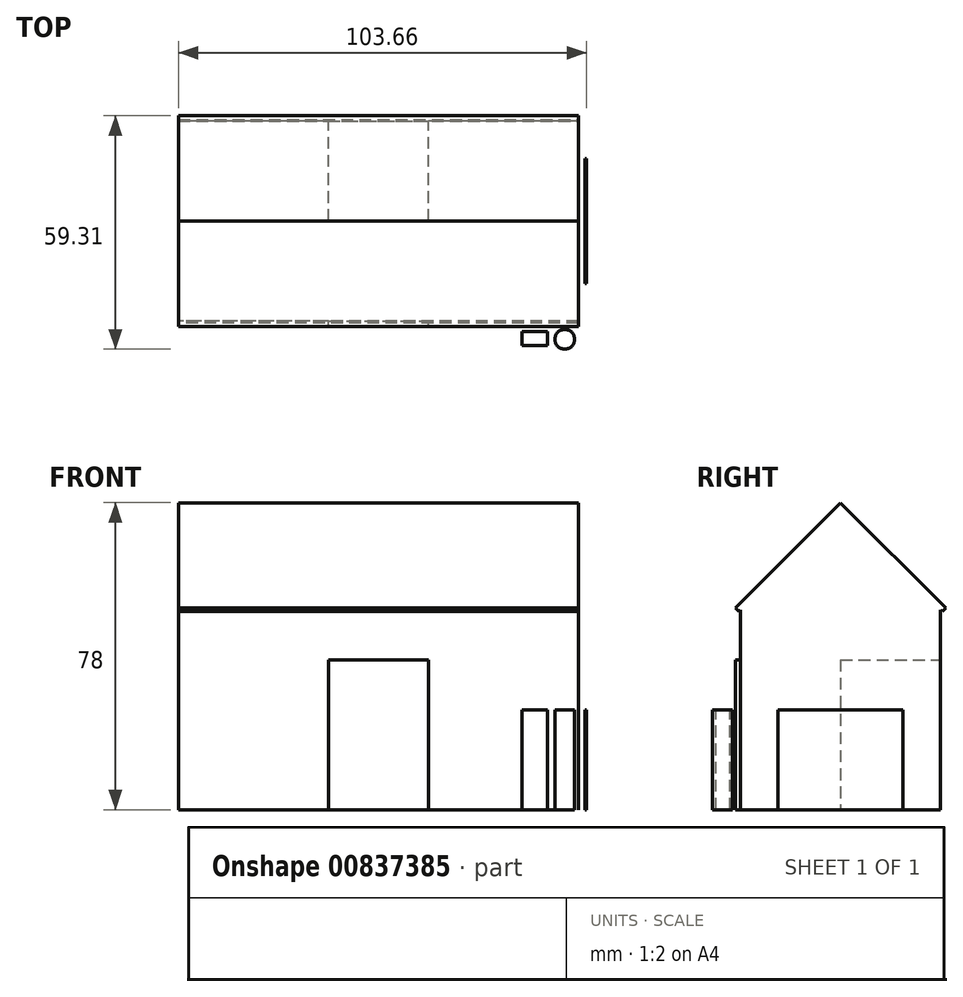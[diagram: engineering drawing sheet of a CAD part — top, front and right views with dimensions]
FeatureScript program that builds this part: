
annotation { "Feature Type Name" : "Feature", "Feature Type Description" : "" }
export const myFeature = defineFeature(function(context is Context, id is Id, definition is map)
    precondition{}
    {
        {
            var Q0;
            Q0=qCreatedBy(makeId("Front.planeOp"),FACE);
            var sketch = newSketch(context, id + "F0", { "sketchPlane" : qUnion([Q0])});
            skLineSegment(sketch, "E0.bottom", {"start": v(50.8, 25.4) * mm, "end": v(-50.8, 25.4) * mm});
            skLineSegment(sketch, "E0.top", {"start": v(50.8, -25.4) * mm, "end": v(-50.8, -25.4) * mm});
            skLineSegment(sketch, "E0.left", {"start": v(50.8, 25.4) * mm, "end": v(50.8, -25.4) * mm});
            skLineSegment(sketch, "E0.right", {"start": v(-50.8, 25.4) * mm, "end": v(-50.8, -25.4) * mm});
            skPoint(sketch, "E0.middle", {"position": v(0, 0) * mm});
            skLineSegment(sketch, "E1.bottom", {"start": v(-50.8, 25.4) * mm, "end": v(50.8, 25.4) * mm});
            skLineSegment(sketch, "E1.top", {"start": v(-50.8, 50.8) * mm, "end": v(50.8, 50.8) * mm});
            skLineSegment(sketch, "E1.left", {"start": v(-50.8, 25.4) * mm, "end": v(-50.8, 50.8) * mm});
            skLineSegment(sketch, "E1.right", {"start": v(50.8, 25.4) * mm, "end": v(50.8, 50.8) * mm});
            skLineSegment(sketch, "E2.bottom", {"start": v(-12.7, 12.7) * mm, "end": v(12.7, 12.7) * mm});
            skLineSegment(sketch, "E3", {"start": v(-12.7, -12.7) * mm, "end": v(-12.7, -25.4) * mm});
            skLineSegment(sketch, "E4", {"start": v(12.7, -12.7) * mm, "end": v(12.7, -25.4) * mm});
            skLineSegment(sketch, "E5", {"start": v(-12.7, 12.7) * mm, "end": v(-12.7, -25.4) * mm});
            skLineSegment(sketch, "E6", {"start": v(12.7, 12.7) * mm, "end": v(12.7, -25.4) * mm});
            skSolve(sketch);
        }
        {
            var Q0;
            Q0=makeQuery(id+"F0.imprint","IMPRINT",FACE,{"disambiguationData":[TD([[makeQuery(id+"F0.imprint","IMPRINT",EDGE,{"derivedFrom":sQuery(id+"F0.wireOp",EDGE,"E0.bottom")}),1.0]])]});
            var Q1;
            Q1=makeQuery(id+"F0.imprint","IMPRINT",FACE,{"disambiguationData":[TD([[makeQuery(id+"F0.imprint","IMPRINT",EDGE,{"derivedFrom":sQuery(id+"F0.wireOp",EDGE,"E0.bottom")}),-1.0]])]});
            extrude(context, id + "F1", {"entities" : qUnion([Q0, Q1]), "endBound" : BoundingType.SYMMETRIC, "depth" : 50.8 * mm, "offsetDistance" : 25.4 * mm});
        }
        {
            var Q0;
            Q0=makeQuery(id+"F1.opExtrude","CAP_EDGE",EDGE,{"disambiguationData":[OSD([sQuery(id+"F0.wireOp",EDGE,"E1.top")])],"isStart":false});
            var Q1;
            Q1=makeQuery(id+"F1.opExtrude","CAP_EDGE",EDGE,{"disambiguationData":[OSD([sQuery(id+"F0.wireOp",EDGE,"E1.top")])],"isStart":true});
            chamfer(context, id + "F2", {"entities" : qUnion([Q0, Q1]), "width" : 25.4 * mm, "tangentPropagation" : true});
        }
        {
            var Q0;
            {var subQ0=sQuery(id+"F0.wireOp",EDGE,"E1.top");Q0=makeQuery(id+"F2.opChamfer","BLEND_FACE",FACE,{"disambiguationData":[OSD([subQ0]),TDD([makeQuery(id+"F1.opExtrude","CAP_EDGE",EDGE,{"disambiguationData":[OSD([subQ0])],"isStart":false})])]});}
            extrude(context, id + "F3", {"entities" : qUnion([Q0]), "operationType" : NewBodyOperationType.ADD, "depth" : 1.27 * mm, "offsetDistance" : 25.4 * mm});
        }
        {
            var Q0;
            {var subQ0=sQuery(id+"F0.wireOp",EDGE,"E1.top");Q0=makeQuery(id+"F3.boolean.opBoolean","MERGE",FACE,{"derivedFrom":[makeQuery(id+"F2.opChamfer","BLEND_FACE",FACE,{"disambiguationData":[OSD([subQ0]),TDD([makeQuery(id+"F1.opExtrude","CAP_EDGE",EDGE,{"disambiguationData":[OSD([subQ0])],"isStart":true})])]}),makeQuery(id+"F3.opExtrude","SWEPT_FACE",FACE,{"disambiguationData":[OSD([subQ0])]})]});}
            extrude(context, id + "F4", {"entities" : qUnion([Q0]), "operationType" : NewBodyOperationType.ADD, "depth" : 1.27 * mm, "offsetDistance" : 25.4 * mm});
        }
        {
            var Q0;
            Q0=makeQuery(id+"F3.opExtrude","SWEPT_FACE",FACE,{"disambiguationData":[OSD([sQuery(id+"F0.wireOp",EDGE,"E0.top"),sQuery(id+"F0.wireOp",EDGE,"E0.left"),sQuery(id+"F0.wireOp",EDGE,"E0.right"),sQuery(id+"F0.wireOp",EDGE,"E1.top"),sQuery(id+"F0.wireOp",EDGE,"E1.left"),sQuery(id+"F0.wireOp",EDGE,"E1.right"),sQuery(id+"F0.wireOp",EDGE,"E2.bottom"),sQuery(id+"F0.wireOp",EDGE,"E3"),sQuery(id+"F0.wireOp",EDGE,"E4"),sQuery(id+"F0.wireOp",EDGE,"E5"),sQuery(id+"F0.wireOp",EDGE,"E6")])]});
            extrude(context, id + "F5", {"entities" : qUnion([Q0]), "operationType" : NewBodyOperationType.ADD, "depth" : 0.64 * mm, "offsetDistance" : 25.4 * mm});
        }
        {
            var Q0;
            Q0=makeQuery(id+"F4.opExtrude","SWEPT_FACE",FACE,{"disambiguationData":[OSD([sQuery(id+"F0.wireOp",EDGE,"E0.top"),sQuery(id+"F0.wireOp",EDGE,"E0.left"),sQuery(id+"F0.wireOp",EDGE,"E0.right"),sQuery(id+"F0.wireOp",EDGE,"E1.top"),sQuery(id+"F0.wireOp",EDGE,"E1.left"),sQuery(id+"F0.wireOp",EDGE,"E1.right"),sQuery(id+"F0.wireOp",EDGE,"E2.bottom"),sQuery(id+"F0.wireOp",EDGE,"E3"),sQuery(id+"F0.wireOp",EDGE,"E4"),sQuery(id+"F0.wireOp",EDGE,"E5"),sQuery(id+"F0.wireOp",EDGE,"E6")])]});
            extrude(context, id + "F6", {"entities" : qUnion([Q0]), "operationType" : NewBodyOperationType.ADD, "depth" : 0.64 * mm, "offsetDistance" : 25.4 * mm});
        }
        {
            var Q0;
            Q0=makeQuery(id+"F0.imprint","IMPRINT",FACE,{"disambiguationData":[TD([[makeQuery(id+"F0.imprint","IMPRINT",EDGE,{"derivedFrom":sQuery(id+"F0.wireOp",EDGE,"E2.bottom")}),-1.0]])]});
            extrude(context, id + "F7", {"entities" : qUnion([Q0]), "operationType" : NewBodyOperationType.ADD, "depth" : 26.67 * mm, "offsetDistance" : 25.4 * mm});
        }
        {
            var Q0;
            Q0=qCreatedBy(makeId("Top.planeOp"),FACE);
            var sketch = newSketch(context, id + "F8", { "sketchPlane" : qUnion([Q0])});
            skLineSegment(sketch, "E7.bottom", {"start": v(52.5, 15.86) * mm, "end": v(52.86, 15.86) * mm});
            skLineSegment(sketch, "E7.top", {"start": v(52.5, -15.86) * mm, "end": v(52.86, -15.86) * mm});
            skLineSegment(sketch, "E7.left", {"start": v(52.5, 15.86) * mm, "end": v(52.5, -15.86) * mm});
            skLineSegment(sketch, "E7.right", {"start": v(52.86, 15.86) * mm, "end": v(52.86, -15.86) * mm});
            skPoint(sketch, "E7.middle", {"position": v(52.68, 0) * mm});
            skLineSegment(sketch, "E8.bottom", {"start": v(36.45, -28.05) * mm, "end": v(43, -28.05) * mm});
            skLineSegment(sketch, "E8.top", {"start": v(36.45, -31.68) * mm, "end": v(43, -31.68) * mm});
            skLineSegment(sketch, "E8.left", {"start": v(36.45, -28.05) * mm, "end": v(36.45, -31.68) * mm});
            skLineSegment(sketch, "E8.right", {"start": v(43, -28.05) * mm, "end": v(43, -31.68) * mm});
            skPoint(sketch, "E8.middle", {"position": v(39.72, -29.86) * mm});
            skCircle(sketch, "E9", {"center": v(47.35, -30.04) * mm, "radius": 2.52 * mm});
            skSolve(sketch);
        }
        {
            var Q0;
            Q0=makeQuery(id+"F8.imprint","IMPRINT",FACE,{"disambiguationData":[TD([[makeQuery(id+"F8.imprint","IMPRINT",EDGE,{"derivedFrom":sQuery(id+"F8.wireOp",EDGE,"E8.bottom")}),-1.0]])]});
            var Q1;
            Q1=makeQuery(id+"F8.imprint","IMPRINT",FACE,{"disambiguationData":[TD([[makeQuery(id+"F8.imprint","IMPRINT",EDGE,{"derivedFrom":sQuery(id+"F8.wireOp",EDGE,"E9")}),1.0]])]});
            extrude(context, id + "F9", {"entities" : qUnion([Q0, Q1]), "oppositeDirection" : true, "depth" : 25.4 * mm, "offsetDistance" : 25.4 * mm});
        }
        {
            var Q0;
            Q0=makeQuery(id+"F8.imprint","IMPRINT",FACE,{"disambiguationData":[TD([[makeQuery(id+"F8.imprint","IMPRINT",EDGE,{"derivedFrom":sQuery(id+"F8.wireOp",EDGE,"E7.bottom")}),-1.0]])]});
            extrude(context, id + "F10", {"entities" : qUnion([Q0]), "oppositeDirection" : true, "depth" : 25.4 * mm, "offsetDistance" : 25.4 * mm});
        }
    });
